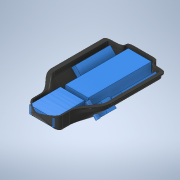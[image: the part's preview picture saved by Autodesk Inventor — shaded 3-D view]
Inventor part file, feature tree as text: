
AUTODESK INVENTOR PART (.ipt)
format: ipt  version: 2020.1 (Build 241239000, 239)  size: 1,989,632 bytes
history: native  units: mm
features: other x30, extrude x10, plane x8, loft x8, surface_op x7, sketch x5, delete_face x1, mirror x1
ambient origin geometry x8: Origin, YZ Plane, XZ Plane, XY Plane, X Axis, Y Axis, Z Axis, Center Point
bodies: Body1 (feature_tree), Body2 (feature_tree), Body3 (feature_tree), Body4 (feature_tree), Body5 (feature_tree), Body6 (feature_tree), Body7 (feature_tree), Body8 (feature_tree), Body9 (feature_tree), Body10 (feature_tree), Body11 (feature_tree), Body12 (feature_tree), Body13 (feature_tree), Body14 (feature_tree), Body15 (feature_tree), Body16 (feature_tree), Body17 (feature_tree)
feature tree (70):
  other  "deck.ipt"
  other  "Battery Pack"
  delete_face  "Delete Face1"
  surface_op  "Extend3"
  plane  "Work Plane1"
  extrude  "Battery Pack Volume"  Depth=300.0mm TaperAngle=0.0deg
  plane  "Work Plane2"
  extrude  "BMS, Anit-Spark, Reiceivers"  Depth=183.3mm
  plane  "Work Plane5"
  extrude  "Right VESC"  Depth=90.0mm TaperAngle=0.0deg
  mirror  "Left VESC"
  plane  "Work Plane3"
  extrude  "XLR Charging slot"  Depth=15.0mm
  extrude  "Power Button"  Depth=102.0mm TaperAngle=0.0deg
  plane  "Work Plane6"
  surface_op  "Extend4"
  other  "++++++ START OF BOX ++++++"
  plane  "Work Plane8"
  plane  "Work Plane9"
  plane  "Work Plane15"
  other  "BOX - Back Profile"
  other  "BOX - Front Profile"
  other  "BOX - End Profile"
  other  "Points"
  surface_op  "Stitch Surface4"
  surface_op  "Stitch Surface5"
  surface_op  "Trim3"
  surface_op  "Trim4"
  surface_op  "Sculpt6"
  other  "Srf1"
  sketch  "Sketch3"  dims[d2=10.0mm d3=300.0mm d4=0.0mm]
  sketch  "Sketch5"  dims[d6=67.0mm d7=183.3mm]
  sketch  "Sketch6"  dims[d8=37.0mm d9=0.0mm d13=90.0mm d14=0.0mm]
  sketch  "Sketch8"  dims[d15=135.0deg d16=15.0mm]
  sketch  "Sketch9"  dims[d17=40.0mm d18=102.0mm d19=0.0mm d20=-5.0mm d28=26.0mm d29=32.0mm d31=10.0mm d32=0.0mm d33=19.0mm d34=0.0mm d35=16.2mm d36=16.2mm d39=33.0mm d40=11.0mm d41=0.0mm d42=0.0mm d43=70.0mm d49=20.0mm d58=3.0mm d66=-41.0mm d67=5.0mm d68=12.0mm d69=-20.0mm d77=-20.0mm d78=0.0mm d79=12.0mm d83=6.0mm d88=2.0mm d91=3.0mm d92=7.0mm d93=3.0mm d94=2.0mm d95=8.0mm d97=150.0mm d98=0.0mm d99=20.0mm d100=0.0mm d110=33.5mm d126=10.0mm d140=21.0mm d151=5.0mm d178=3.0mm d179=4.0mm d182=3.0mm d183=3.0mm d185=5.0mm d186=2.0mm d187=3.0mm d200=150.0mm d201=0.0mm d202=20.0mm d203=0.0mm d212=7.0mm d213=90.0deg d220=10.0mm d221=90.0deg d222=10.0mm d223=90.0deg d224=15.0mm d225=90.0deg d226=10.0mm d227=90.0deg d240=10.0mm d241=90.0deg d242=20.0mm d243=90.0deg d248=10.0mm d249=90.0deg d250=11.0mm d251=90.0deg d257=30.0mm d258=8.0mm d259=15.0mm d260=11.0mm d263=12.0mm d264=6.0mm d265=3.0mm d266=23.0mm d269=6.0mm d270=6.0mm d271=4.0mm d272=10.0mm d273=90.0deg d274=25.0mm d275=90.0deg d278=10.0mm d279=90.0deg d280=5.0mm d281=90.0deg d282=3.0mm d283=-18.0mm d284=7.0mm d285=90.0deg d286=0.0mm d287=90.0deg d288=0.0mm d289=90.0deg]
  other  "Front Profile"
  other  "Srf2"
  other  "Srf3"
  other  "Srf16"
  other  "Srf17"
  other  "Srf20"
  other  "Srf21"
  other  "Srf22"
  other  "Srf23"
  other  "Edges15"
  other  "Edges16"
  other  "Edges13"
  other  "Edges14"
  other  "Srf26"
  other  "Srf27"
  other  "Srf28"
  other  "Srf29"
  other  "Srf30"
  other  "Srf31"
  other  "Edges17"
  other  "Edges18"
  other  "Box"
  extrude  "ExtrusionSrf1"  [1 undecoded]
  extrude  "ExtrusionSrf2"  Depth=26.0mm
  extrude  "ExtrusionSrf3"  Depth=32.0mm
  extrude  "ExtrusionSrf7"  Depth=10.0mm TaperAngle=0.0deg
  extrude  "ExtrusionSrf8"  Depth=19.0mm TaperAngle=0.0deg
  loft  "LoftSrf8"
  loft  "LoftSrf9"
  loft  "LoftSrf10"
  loft  "LoftSrf11"
  loft  "LoftSrf12"
  loft  "LoftSrf13"
  loft  "LoftSrf14"
  loft  "LoftSrf15"
note: 1 required parameter value undecoded (feature->parameter linkage not recoverable at this tier; creation-order binding heuristic only, values carry confidence <= 0.55)
